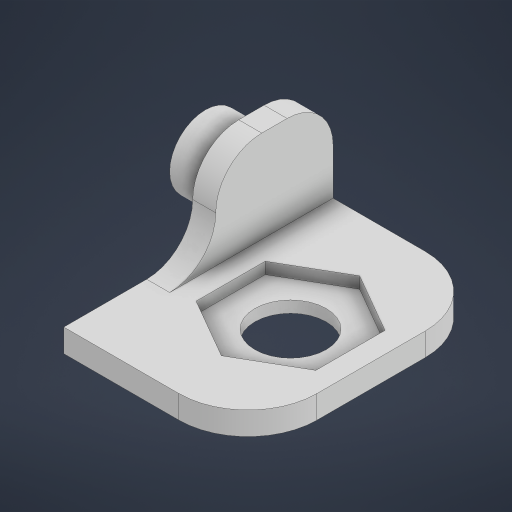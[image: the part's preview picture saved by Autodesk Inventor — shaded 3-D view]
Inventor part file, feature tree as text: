
AUTODESK INVENTOR PART (.ipt)
format: ipt  version: 2024 (Build 280153000, 153)  size: 266,240 bytes
history: native  units: in
note: dims shown in document units (in); Inventor stores cm internally (conversion verified against a paired STEP export)
features: sketch x5, extrude x4, fillet x3, hole x1
ambient origin geometry x8: Origin, YZ Plane, XZ Plane, XY Plane, X Axis, Y Axis, Z Axis, Center Point
bodies: Solid1 (feature_tree)
feature tree (13):
  extrude  "Extrusion1"  Depth=0.1969in
  extrude  "Extrusion2"  Depth=0.4213in TaperAngle=0.0deg
  hole  "Hole1"  [1 undecoded]
  sketch  "Sketch4"  dims[d9=0.0787in d10=0.0in d11=0.1378in d12=0.2106in]
  fillet  "Fillet1"  Radius=0.0394in
  extrude  "Extrusion3"  Depth=0.0787in
  fillet  "Fillet3"  Radius=0.2106in
  extrude  "Extrusion4"  Depth=0.0787in
  fillet  "Fillet4"  Radius=0.1181in
  sketch  "Sketch1"  dims[d0=0.315in d1=0.1969in]
  sketch  "Sketch2"  dims[d2=0.0394in d3=0.4213in d4=0.0in]
  sketch  "Sketch3"  dims[d5=0.122in d6=0.1004in d8=0.0394in]
  sketch  "Sketch5"  dims[d13=0.122in d14=0.2362in d15=0.1575in d16=0.0787in d17=90.0deg d18=0.315in d19=0.8108in d20=0.2366in d21=0.1181in d22=0.0197in d23=0.0in d28=0.1004in d30=0.0787in d31=0.1575in d32=0.1004in d33=0.0394in d34=0.0in d35=0.0787in d24=0.0344in]
note: 1 required parameter value undecoded (feature->parameter linkage not recoverable at this tier; creation-order binding heuristic only, values carry confidence <= 0.55)
